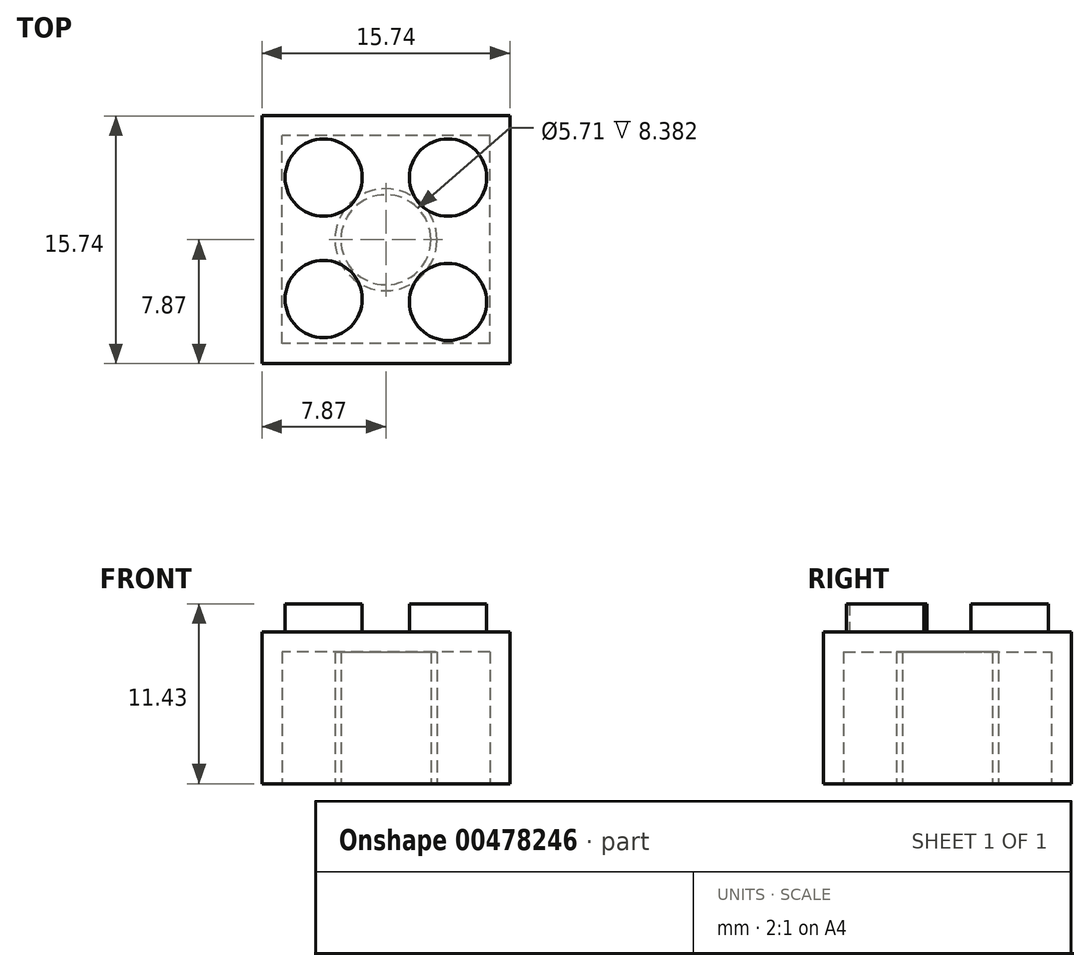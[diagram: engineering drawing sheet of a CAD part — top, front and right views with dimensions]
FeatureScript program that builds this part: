
annotation { "Feature Type Name" : "Feature", "Feature Type Description" : "" }
export const myFeature = defineFeature(function(context is Context, id is Id, definition is map)
    precondition{}
    {
        {
            var Q0;
            Q0=qCreatedBy(makeId("Top.planeOp"),FACE);
            var sketch = newSketch(context, id + "F0", { "sketchPlane" : qUnion([Q0])});
            skLineSegment(sketch, "E0.bottom", {"start": v(7.87, -7.87) * mm, "end": v(-7.87, -7.87) * mm});
            skLineSegment(sketch, "E0.top", {"start": v(7.87, 7.87) * mm, "end": v(-7.87, 7.87) * mm});
            skLineSegment(sketch, "E0.left", {"start": v(7.87, -7.87) * mm, "end": v(7.87, 7.87) * mm});
            skLineSegment(sketch, "E0.right", {"start": v(-7.87, -7.87) * mm, "end": v(-7.87, 7.87) * mm});
            skPoint(sketch, "E0.middle", {"position": v(0, 0) * mm});
            skSolve(sketch);
        }
        {
            var Q0;
            Q0 = qSketchRegion(id + "F0", true);
            extrude(context, id + "F1", {"entities" : qUnion([Q0]), "depth" : 9.65 * mm, "offsetDistance" : 25.4 * mm});
        }
        {
            var Q0;
            Q0=makeQuery(id+"F1.opExtrude","CAP_FACE",FACE,{"disambiguationData":[OSD([sQuery(id+"F0.wireOp",EDGE,"E0.bottom"),sQuery(id+"F0.wireOp",EDGE,"E0.top"),sQuery(id+"F0.wireOp",EDGE,"E0.left"),sQuery(id+"F0.wireOp",EDGE,"E0.right")])],"isStart":false});
            var sketch = newSketch(context, id + "F2", { "sketchPlane" : qUnion([Q0])});
            skCircle(sketch, "E1", {"center": v(-3.95, 3.95) * mm, "radius": 2.45 * mm});
            skCircle(sketch, "E2", {"center": v(3.95, 3.95) * mm, "radius": 2.45 * mm});
            skCircle(sketch, "E3", {"center": v(-3.95, -3.77) * mm, "radius": 2.45 * mm});
            skCircle(sketch, "E4", {"center": v(3.95, -3.95) * mm, "radius": 2.45 * mm});
            skSolve(sketch);
        }
        {
            var Q0;
            Q0 = qSketchRegion(id + "F2", true);
            extrude(context, id + "F3", {"entities" : qUnion([Q0]), "operationType" : NewBodyOperationType.ADD, "depth" : 1.78 * mm});
        }
        {
            var Q0;
            Q0=makeQuery(id+"F1.opExtrude","CAP_FACE",FACE,{"disambiguationData":[OSD([sQuery(id+"F0.wireOp",EDGE,"E0.bottom"),sQuery(id+"F0.wireOp",EDGE,"E0.top"),sQuery(id+"F0.wireOp",EDGE,"E0.left"),sQuery(id+"F0.wireOp",EDGE,"E0.right")])],"isStart":true});
            var sketch = newSketch(context, id + "F4", { "sketchPlane" : qUnion([Q0])});
            skLineSegment(sketch, "E5.bottom", {"start": v(6.6, 6.6) * mm, "end": v(-6.6, 6.6) * mm});
            skLineSegment(sketch, "E5.top", {"start": v(6.6, -6.6) * mm, "end": v(-6.6, -6.6) * mm});
            skLineSegment(sketch, "E5.left", {"start": v(6.6, 6.6) * mm, "end": v(6.6, -6.6) * mm});
            skLineSegment(sketch, "E5.right", {"start": v(-6.6, 6.6) * mm, "end": v(-6.6, -6.6) * mm});
            skPoint(sketch, "E5.middle", {"position": v(0, 0) * mm});
            skSolve(sketch);
        }
        {
            var Q0;
            Q0=makeQuery(id+"F4.imprint","IMPRINT",FACE,{"disambiguationData":[TD([[makeQuery(id+"F4.imprint","IMPRINT",EDGE,{"derivedFrom":sQuery(id+"F4.wireOp",EDGE,"E5.bottom")}),1.0]])]});
            var sketch = newSketch(context, id + "F5", { "sketchPlane" : qUnion([Q0])});
            skCircle(sketch, "E6", {"center": v(0, 0) * mm, "radius": 3.24 * mm});
            skCircle(sketch, "E7", {"center": v(0, 0) * mm, "radius": 2.86 * mm});
            skSolve(sketch);
        }
        {
            var Q0;
            Q0 = qSketchRegion(id + "F4", true);
            extrude(context, id + "F6", {"entities" : qUnion([Q0]), "operationType" : NewBodyOperationType.REMOVE, "oppositeDirection" : true, "depth" : 8.38 * mm, "offsetDistance" : 25.4 * mm});
        }
        {
            var Q0;
            Q0 = qSketchRegion(id + "F5", true);
            extrude(context, id + "F7", {"entities" : qUnion([Q0]), "operationType" : NewBodyOperationType.ADD, "oppositeDirection" : true, "depth" : 8.38 * mm, "offsetDistance" : 25.4 * mm});
        }
    });
